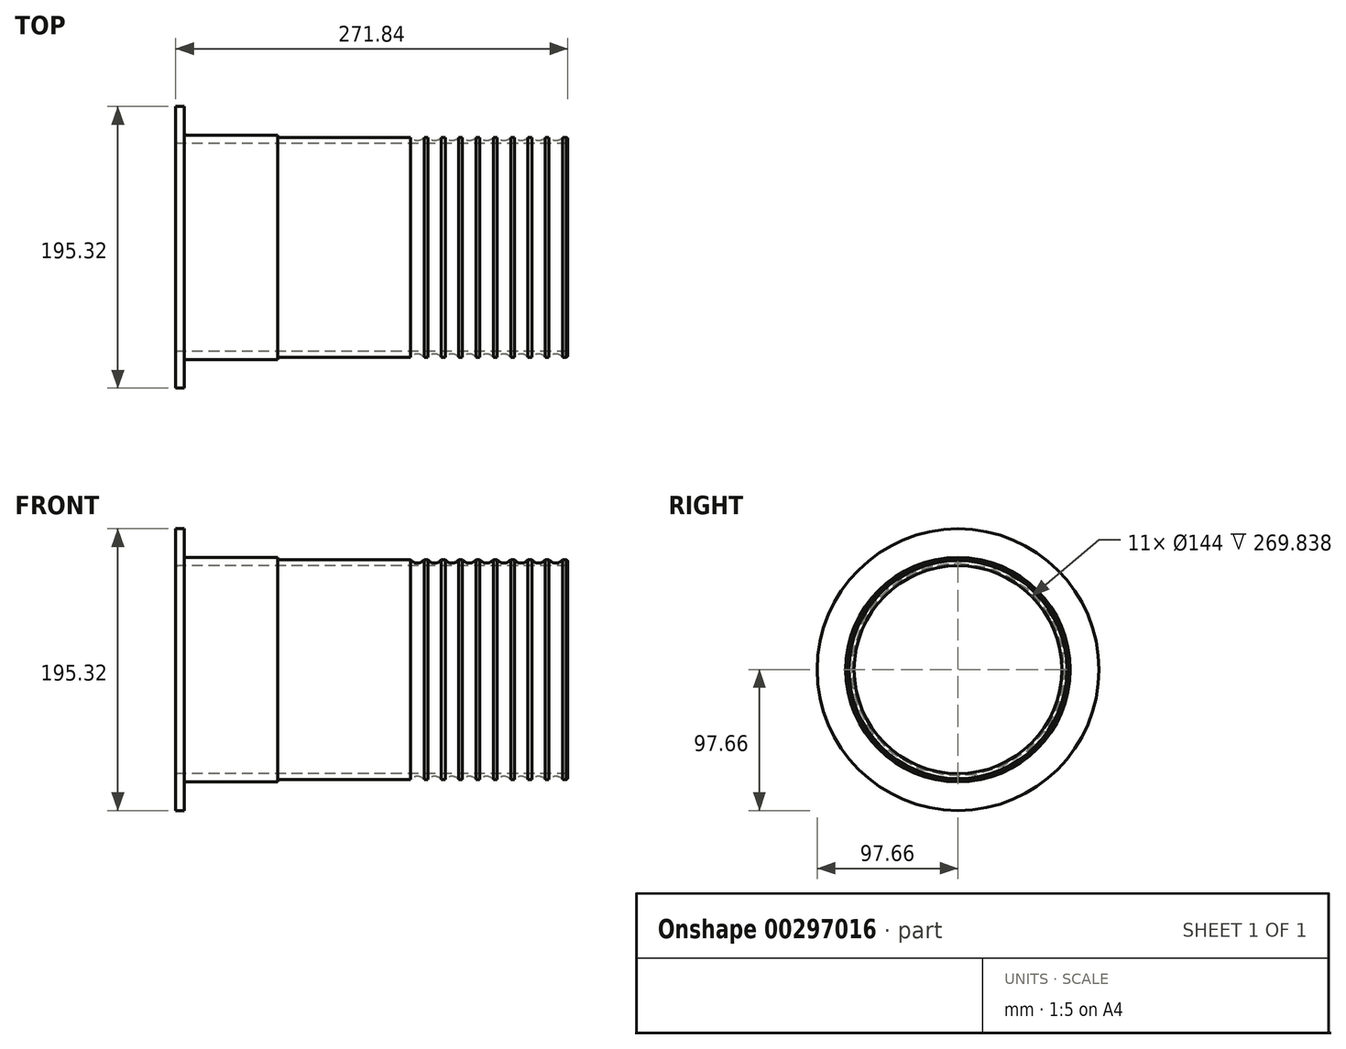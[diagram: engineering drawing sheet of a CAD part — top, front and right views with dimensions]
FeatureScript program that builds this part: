
annotation { "Feature Type Name" : "Feature", "Feature Type Description" : "" }
export const myFeature = defineFeature(function(context is Context, id is Id, definition is map)
    precondition{}
    {
        {
            var Q0;
            Q0=qCreatedBy(makeId("Front.planeOp"),FACE);
            var sketch = newSketch(context, id + "F0", { "sketchPlane" : qUnion([Q0])});
            skLineSegment(sketch, "E0", {"start": v(-0.84, -4.15) * mm, "end": v(269, -4.15) * mm});
            skLineSegment(sketch, "E1", {"start": v(269, -4.15) * mm, "end": v(269, 60.01) * mm, "construction": true});
            skLineSegment(sketch, "E2", {"start": v(269, 0.76) * mm, "end": v(269, -4.15) * mm});
            skArc(sketch, "E3", {"start": v(160, 0) * mm, "mid": v(164.68, -2.25) * mm, "end": v(169.37, 0) * mm});
            skPoint(sketch, "E4.endSnap0", {"position": v(164.68, -2.25) * mm});
            skArc(sketch, "E5.1.0.0", {"start": v(172, 0) * mm, "mid": v(176.68, -2.25) * mm, "end": v(181.37, 0) * mm});
            skArc(sketch, "E5.2.0.0", {"start": v(184, 0) * mm, "mid": v(188.68, -2.25) * mm, "end": v(193.37, 0) * mm});
            skArc(sketch, "E5.3.0.0", {"start": v(196, 0) * mm, "mid": v(200.68, -2.25) * mm, "end": v(205.37, 0) * mm});
            skArc(sketch, "E5.4.0.0", {"start": v(208, 0) * mm, "mid": v(212.68, -2.25) * mm, "end": v(217.37, 0) * mm});
            skArc(sketch, "E5.5.0.0", {"start": v(220, 0) * mm, "mid": v(224.68, -2.25) * mm, "end": v(229.37, 0) * mm});
            skArc(sketch, "E5.6.0.0", {"start": v(232, 0) * mm, "mid": v(236.68, -2.25) * mm, "end": v(241.37, 0) * mm});
            skArc(sketch, "E5.7.0.0", {"start": v(244, 0) * mm, "mid": v(248.68, -2.25) * mm, "end": v(253.37, 0) * mm});
            skArc(sketch, "E5.8.0.0", {"start": v(256, 0) * mm, "mid": v(260.68, -2.25) * mm, "end": v(265.37, 0) * mm});
            skLineSegment(sketch, "E6", {"start": v(169.37, 0) * mm, "end": v(172, 0) * mm});
            skLineSegment(sketch, "E7.1.0.0", {"start": v(181.37, 0) * mm, "end": v(184, 0) * mm});
            skLineSegment(sketch, "E7.2.0.0", {"start": v(193.37, 0) * mm, "end": v(196, 0) * mm});
            skLineSegment(sketch, "E7.3.0.0", {"start": v(205.37, 0) * mm, "end": v(208, 0) * mm});
            skLineSegment(sketch, "E7.4.0.0", {"start": v(217.37, 0) * mm, "end": v(220, 0) * mm});
            skLineSegment(sketch, "E7.5.0.0", {"start": v(229.37, 0) * mm, "end": v(232, 0) * mm});
            skLineSegment(sketch, "E7.6.0.0", {"start": v(241.37, 0) * mm, "end": v(244, 0) * mm});
            skLineSegment(sketch, "E7.7.0.0", {"start": v(253.37, 0) * mm, "end": v(256, 0) * mm});
            skLineSegment(sketch, "E7.8.0.0", {"start": v(265.37, 0) * mm, "end": v(268, 0) * mm});
            skLineSegment(sketch, "E8", {"start": v(-12.74, -76.15) * mm, "end": v(290.26, -76.15) * mm, "construction": true});
            skArc(sketch, "E9.1.0.0", {"start": v(268, 0) * mm, "mid": v(268.48, -0.33) * mm, "end": v(269, -0.62) * mm});
            skLineSegment(sketch, "E10", {"start": v(160, 0) * mm, "end": v(67.84, 0) * mm});
            skLineSegment(sketch, "E11", {"start": v(67.84, 0) * mm, "end": v(67.84, 1.65) * mm});
            skLineSegment(sketch, "E12", {"start": v(67.84, 1.65) * mm, "end": v(5, 1.65) * mm});
            skLineSegment(sketch, "E13", {"start": v(3, 3.65) * mm, "end": v(3, 21.51) * mm});
            skLineSegment(sketch, "E14", {"start": v(3, 21.51) * mm, "end": v(-2.84, 21.51) * mm});
            skLineSegment(sketch, "E15", {"start": v(-2.84, 21.51) * mm, "end": v(-2.84, -2.15) * mm});
            skPoint(sketch, "E16.visualSharp", {"position": v(3, 1.65) * mm});
            skArc(sketch, "E16.filletArc", {"start": v(3, 3.65) * mm, "mid": v(3.59, 2.24) * mm, "end": v(5, 1.65) * mm});
            skPoint(sketch, "E17.visualSharp", {"position": v(-2.84, -4.15) * mm});
            skArc(sketch, "E17.filletArc", {"start": v(-2.84, -2.15) * mm, "mid": v(-2.25, -3.56) * mm, "end": v(-0.84, -4.15) * mm});
            skSolve(sketch);
        }
        {
            var Q0;
            {var subQ2=sQuery(id+"F0.wireOp",EDGE,"E0");Q0=makeQuery(id+"F0.imprint","IMPRINT",FACE,{"disambiguationData":[TD([[makeQuery(id+"F0.imprint","IMPRINT",EDGE,{"derivedFrom":subQ2}),1.0]])]});}
            var Q1;
            Q1=sQuery(id+"F0.wireOp",EDGE,"E8");
            revolve(context, id + "F1", {"entities" : qUnion([Q0]), "axis" : qUnion([Q1]), "revolveType" : RevolveType.FULL});
        }
    });
